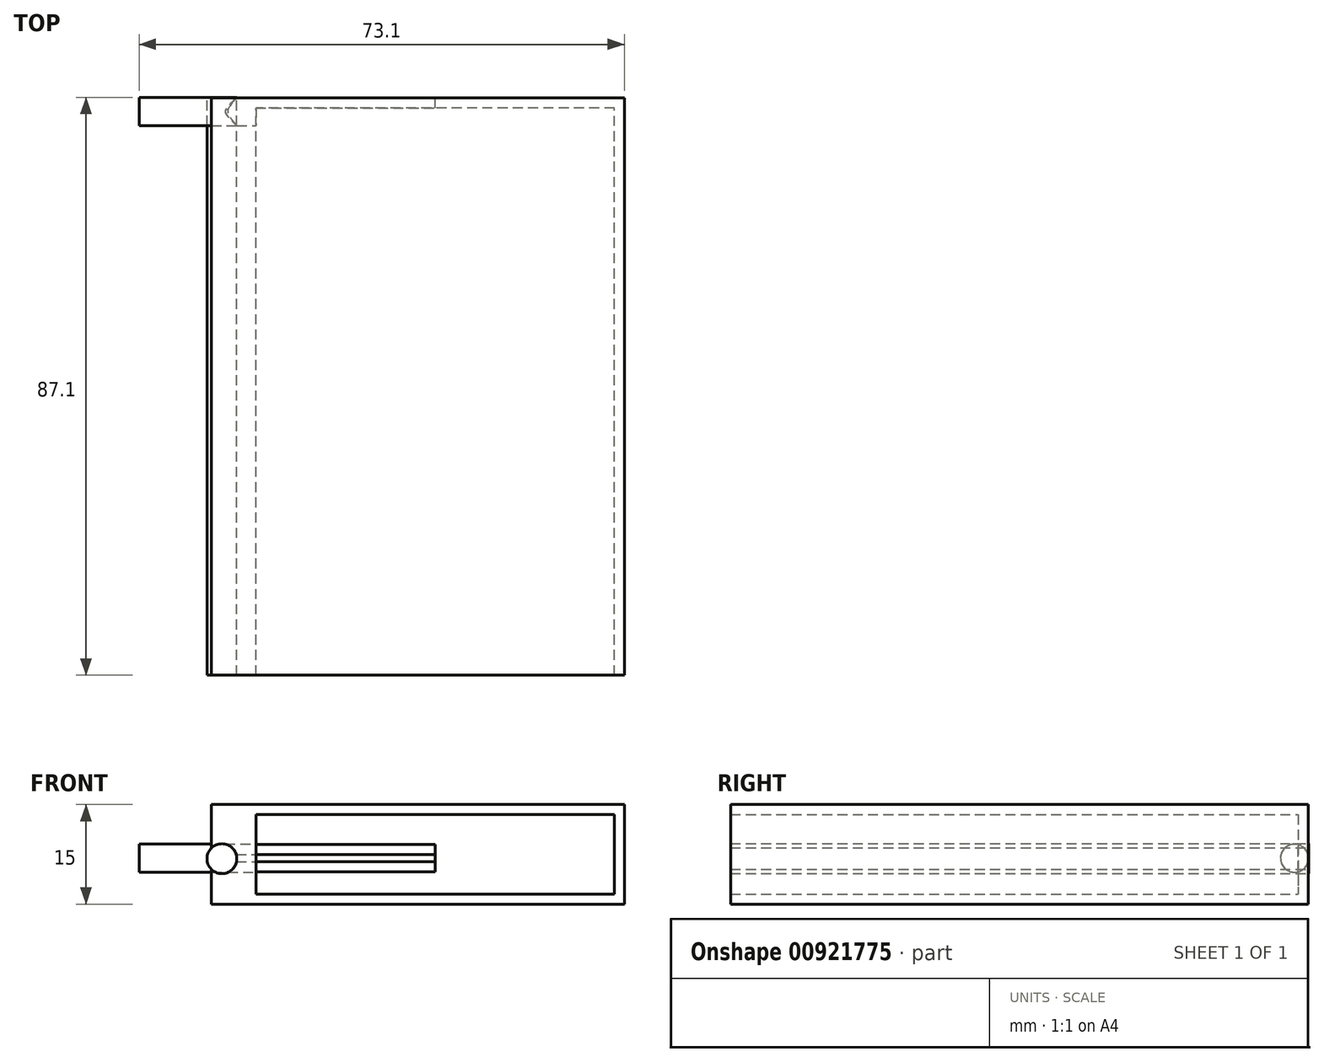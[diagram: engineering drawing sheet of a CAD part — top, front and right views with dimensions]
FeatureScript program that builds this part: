
annotation { "Feature Type Name" : "Feature", "Feature Type Description" : "" }
export const myFeature = defineFeature(function(context is Context, id is Id, definition is map)
    precondition{}
    {
        {
            var Q0;
            Q0=qCreatedBy(makeId("Top.planeOp"),FACE);
            var sketch = newSketch(context, id + "F0", { "sketchPlane" : qUnion([Q0])});
            skLineSegment(sketch, "E0.bottom", {"start": v(28.5, -43.5) * mm, "end": v(-28.5, -43.5) * mm});
            skLineSegment(sketch, "E0.top", {"start": v(28.5, 43.5) * mm, "end": v(-28.5, 43.5) * mm});
            skLineSegment(sketch, "E0.left", {"start": v(28.5, -43.5) * mm, "end": v(28.5, 43.5) * mm});
            skLineSegment(sketch, "E0.right", {"start": v(-28.5, -43.5) * mm, "end": v(-28.5, 43.5) * mm});
            skPoint(sketch, "E0.middle", {"position": v(0, 0) * mm});
            skSolve(sketch);
        }
        {
            var Q0;
            Q0 = qSketchRegion(id + "F0", true);
            extrude(context, id + "F1", {"entities" : qUnion([Q0]), "depth" : 15 * mm, "offsetDistance" : 25 * mm});
        }
        {
            var Q0;
            Q0=makeQuery(id+"F1.opExtrude","SWEPT_BODY",BODY,{"disambiguationData":[OSD([sQuery(id+"F0.wireOp",EDGE,"E0.bottom"),sQuery(id+"F0.wireOp",EDGE,"E0.top"),sQuery(id+"F0.wireOp",EDGE,"E0.left"),sQuery(id+"F0.wireOp",EDGE,"E0.right")])]});
            transform(context, id + "F2", {"entities" : qUnion([Q0]), "transformType" : TransformType.TRANSLATION_3D, "dx" : 0 * mm, "dy" : 0 * mm, "dz" : -7.5 * mm, "makeCopy" : false});
        }
        {
            var Q0;
            Q0=makeQuery(id+"F1.opExtrude","SWEPT_BODY",BODY,{"disambiguationData":[OSD([sQuery(id+"F0.wireOp",EDGE,"E0.bottom"),sQuery(id+"F0.wireOp",EDGE,"E0.top"),sQuery(id+"F0.wireOp",EDGE,"E0.left"),sQuery(id+"F0.wireOp",EDGE,"E0.right")])]});
            transform(context, id + "F3", {"entities" : qUnion([Q0]), "transformType" : TransformType.TRANSLATION_3D, "dx" : 0 * mm, "dy" : 0 * mm, "dz" : 7.5 * mm, "makeCopy" : false});
        }
        {
            var Q0;
            Q0=makeQuery(id+"F1.opExtrude","SWEPT_FACE",FACE,{"disambiguationData":[OSD([sQuery(id+"F0.wireOp",EDGE,"E0.bottom")])]});
            shell(context, id + "F4", {"entities" : qUnion([Q0]), "thickness" : 1.5 * mm});
        }
        {
            var Q0;
            Q0=makeQuery(id+"F1.opExtrude","SWEPT_FACE",FACE,{"disambiguationData":[OSD([sQuery(id+"F0.wireOp",EDGE,"E0.right")])]});
            extrude(context, id + "F5", {"entities" : qUnion([Q0]), "operationType" : NewBodyOperationType.ADD, "depth" : 5.2 * mm, "offsetDistance" : 25 * mm});
        }
        {
            var Q0;
            Q0=qCreatedBy(makeId("Front.planeOp"),FACE);
            var sketch = newSketch(context, id + "F6", { "sketchPlane" : qUnion([Q0])});
            skCircle(sketch, "E1", {"center": v(-31.03, 7.44) * mm, "radius": 2.25 * mm});
            skSolve(sketch);
        }
        {
            var Q0;
            Q0=makeQuery(id+"F6.imprint","IMPRINT",FACE,{"disambiguationData":[TD([[makeQuery(id+"F6.imprint","IMPRINT",EDGE,{"derivedFrom":sQuery(id+"F6.wireOp",EDGE,"E1")}),1.0]])]});
            extrude(context, id + "F7", {"entities" : qUnion([Q0]), "endBound" : BoundingType.THROUGH_ALL, "depth" : 25 * mm, "offsetDistance" : 25 * mm, "hasSecondDirection" : true, "secondDirectionBound" : SecondDirectionBoundingType.THROUGH_ALL, "secondDirectionOppositeDirection" : true, "secondDirectionDepth" : 25 * mm});
        }
        {
            var Q0;
            Q0=makeQuery(id+"F7.opExtrude","SWEPT_BODY",BODY,{"disambiguationData":[OSD([sQuery(id+"F6.wireOp",EDGE,"E1")])]});
            transform(context, id + "F8", {"entities" : qUnion([Q0]), "transformType" : TransformType.TRANSLATION_3D, "dx" : -1.1 * mm, "dy" : 0 * mm, "dz" : 0 * mm, "makeCopy" : false});
        }
        {
            var Q0;
            Q0=makeQuery(id+"F7.opExtrude","SWEPT_BODY",BODY,{"disambiguationData":[OSD([sQuery(id+"F6.wireOp",EDGE,"E1")])]});
            transform(context, id + "F9", {"entities" : qUnion([Q0]), "transformType" : TransformType.TRANSLATION_3D, "dx" : 0 * mm, "dy" : 0 * mm, "dz" : -0.6 * mm, "makeCopy" : false});
        }
        {
            var Q0;
            Q0=makeQuery(id+"F7.opExtrude","SWEPT_BODY",BODY,{"disambiguationData":[OSD([sQuery(id+"F6.wireOp",EDGE,"E1")])]});
            var Q1;
            Q1=makeQuery(id+"F1.opExtrude","SWEPT_BODY",BODY,{"disambiguationData":[OSD([sQuery(id+"F0.wireOp",EDGE,"E0.bottom"),sQuery(id+"F0.wireOp",EDGE,"E0.top"),sQuery(id+"F0.wireOp",EDGE,"E0.left"),sQuery(id+"F0.wireOp",EDGE,"E0.right")])]});
            booleanBodies(context, id + "F10", {"operationType" : BooleanOperationType.SUBTRACTION, "tools" : qUnion([Q0]), "targets" : qUnion([Q1]), "keepTools" : true});
        }
        {
            var Q0;
            Q0=makeQuery(id+"F7.opExtrude","CAP_FACE",FACE,{"disambiguationData":[OSD([sQuery(id+"F6.wireOp",EDGE,"E1")])],"isStart":false});
            var Q1;
            Q1=sQuery(id+"F0.wireOp",VERTEX,"E0.bottom.end");
            extrude(context, id + "F11", {"entities" : qUnion([Q0]), "operationType" : NewBodyOperationType.REMOVE, "endBound" : BoundingType.UP_TO_VERTEX, "oppositeDirection" : true, "depth" : 25 * mm, "endBoundEntityVertex" : qUnion([Q1]), "offsetDistance" : 25 * mm});
        }
        {
            var Q0;
            Q0=makeQuery(id+"F7.opExtrude","CAP_FACE",FACE,{"disambiguationData":[OSD([sQuery(id+"F6.wireOp",EDGE,"E1")])],"isStart":true});
            extrude(context, id + "F12", {"entities" : qUnion([Q0]), "operationType" : NewBodyOperationType.REMOVE, "oppositeDirection" : true, "depth" : 64.4 * mm, "offsetDistance" : 25 * mm});
        }
        {
            var Q0;
            Q0=makeQuery(id+"F7.opExtrude","SWEPT_BODY",BODY,{"disambiguationData":[OSD([sQuery(id+"F6.wireOp",EDGE,"E1")])]});
            transform(context, id + "F13", {"entities" : qUnion([Q0]), "transformType" : TransformType.TRANSLATION_3D, "dx" : 0 * mm, "dy" : 0 * mm, "dz" : 0 * mm, "makeCopy" : true});
        }
        {
            var Q0;
            Q0=makeQuery(id+"F13.opPattern","COPY",BODY,{"derivedFrom":makeQuery(id+"F7.opExtrude","SWEPT_BODY",BODY,{"disambiguationData":[OSD([sQuery(id+"F6.wireOp",EDGE,"E1")])]}),"instanceName":"1"});
            deleteBodies(context, id + "F14", {"entities" : qUnion([Q0])});
        }
        {
            var Q0;
            Q0=makeQuery(id+"F7.opExtrude","SWEPT_BODY",BODY,{"disambiguationData":[OSD([sQuery(id+"F6.wireOp",EDGE,"E1")])]});
            transform(context, id + "F15", {"entities" : qUnion([Q0]), "transformType" : TransformType.TRANSLATION_3D, "dx" : 10 * mm, "dy" : 10 * mm, "dz" : 30 * mm, "makeCopy" : true});
        }
        {
            var Q0;
            Q0=makeQuery(id+"F15.opPattern","COPY",BODY,{"derivedFrom":makeQuery(id+"F7.opExtrude","SWEPT_BODY",BODY,{"disambiguationData":[OSD([sQuery(id+"F6.wireOp",EDGE,"E1")])]}),"instanceName":"1"});
            deleteBodies(context, id + "F16", {"entities" : qUnion([Q0])});
        }
        {
            var Q0;
            Q0=qCreatedBy(makeId("Right.planeOp"),FACE);
            var sketch = newSketch(context, id + "F17", { "sketchPlane" : qUnion([Q0])});
            skCircle(sketch, "E2", {"center": v(41.45, 6.91) * mm, "radius": 2.12 * mm});
            skPoint(sketch, "E2.first.point", {"position": v(43.57, 7) * mm});
            skPoint(sketch, "E2.second.point", {"position": v(39.32, 6.82) * mm});
            skPoint(sketch, "E2.third.point", {"position": v(41.45, 9.04) * mm});
            skCircle(sketch, "E3", {"center": v(-41.47, 7.05) * mm, "radius": 2 * mm});
            skPoint(sketch, "E3.first.point", {"position": v(-43.47, 7) * mm});
            skPoint(sketch, "E3.second.point", {"position": v(-39.47, 7) * mm});
            skPoint(sketch, "E3.third.point", {"position": v(-41.72, 9.04) * mm});
            skSolve(sketch);
        }
        {
            var Q0;
            Q0=makeQuery(id+"F17.imprint","IMPRINT",FACE,{"disambiguationData":[TD([[makeQuery(id+"F17.imprint","IMPRINT",EDGE,{"derivedFrom":sQuery(id+"F17.wireOp",EDGE,"E2")}),1.0]])]});
            var Q1;
            Q1=sQuery(id+"F17.wireOp",EDGE,"E2");
            extrude(context, id + "F18", {"entities" : qUnion([Q0]), "surfaceEntities" : qUnion([Q1]), "oppositeDirection" : true, "depth" : 44.6 * mm, "offsetDistance" : 25 * mm});
        }
        {
            var Q0;
            Q0=makeQuery(id+"F18.opExtrude","CAP_FACE",FACE,{"disambiguationData":[OSD([sQuery(id+"F17.wireOp",EDGE,"E2")])],"isStart":true});
            var Q1;
            Q1=makeQuery(id+"F7.opExtrude","SWEPT_FACE",FACE,{"disambiguationData":[OSD([sQuery(id+"F6.wireOp",EDGE,"E1")])]});
            extrude(context, id + "F19", {"entities" : qUnion([Q0]), "operationType" : NewBodyOperationType.REMOVE, "endBound" : BoundingType.UP_TO_SURFACE, "oppositeDirection" : true, "depth" : 25 * mm, "endBoundEntityFace" : qUnion([Q1]), "offsetDistance" : 25 * mm});
        }
    });
